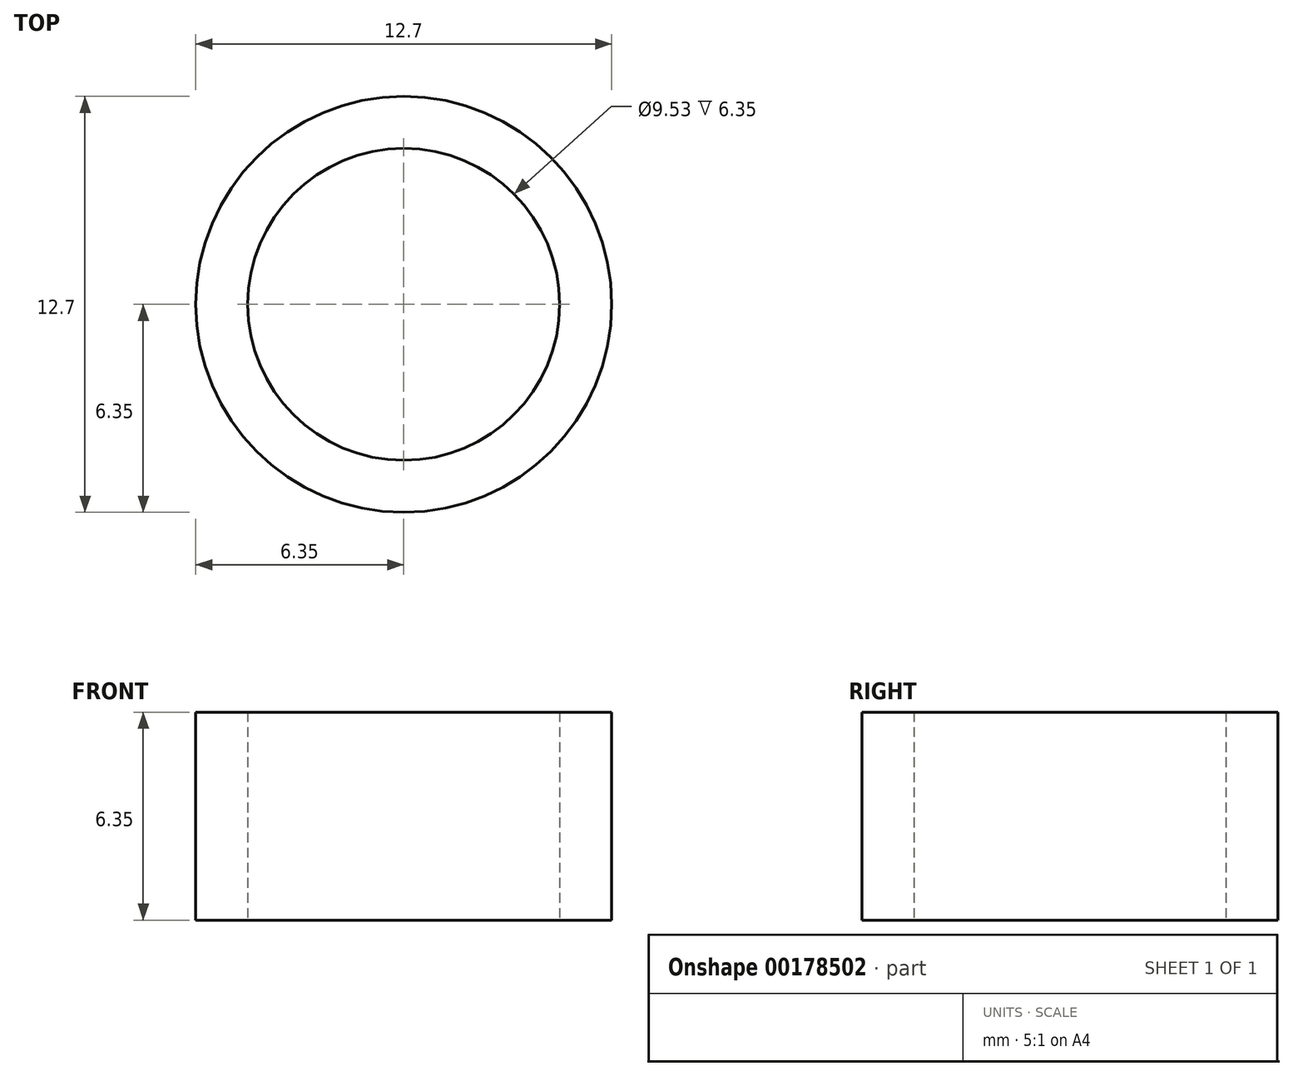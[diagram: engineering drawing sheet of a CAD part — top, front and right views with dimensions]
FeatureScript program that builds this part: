
annotation { "Feature Type Name" : "Feature", "Feature Type Description" : "" }
export const myFeature = defineFeature(function(context is Context, id is Id, definition is map)
    precondition{}
    {
        {
            var Q0;
            Q0=qCreatedBy(makeId("Top.planeOp"),FACE);
            var sketch = newSketch(context, id + "F0", { "sketchPlane" : qUnion([Q0])});
            skCircle(sketch, "E0", {"center": v(0, 0) * mm, "radius": 6.35 * mm});
            skCircle(sketch, "E1", {"center": v(0, 0) * mm, "radius": 4.76 * mm});
            skSolve(sketch);
        }
        {
            var Q0;
            Q0=makeQuery(id+"F0.imprint","IMPRINT",FACE,{"disambiguationData":[TD([[makeQuery(id+"F0.imprint","IMPRINT",EDGE,{"derivedFrom":sQuery(id+"F0.wireOp",EDGE,"E0")}),1.0]])]});
            extrude(context, id + "F1", {"entities" : qUnion([Q0]), "depth" : 6.35 * mm});
        }
    });
